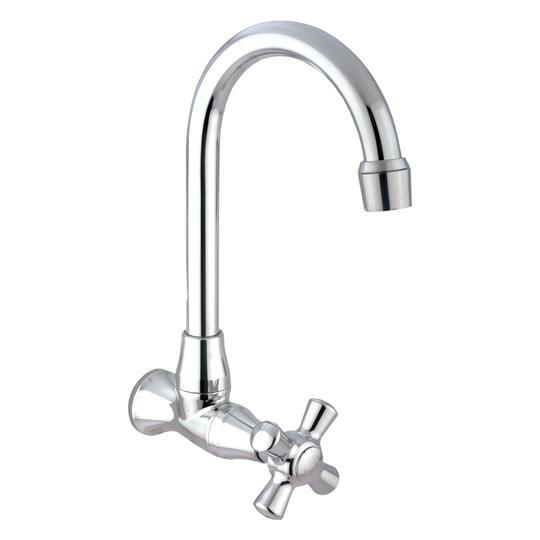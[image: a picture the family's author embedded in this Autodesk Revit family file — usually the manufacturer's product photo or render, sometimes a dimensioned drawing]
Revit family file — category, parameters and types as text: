
# Revit family: 01-0944-11 LLAVE MOVIL PARED HELVETIA
name_source: partatom
category: Plumbing Fixtures
revit_build: Autodesk Revit 2018 (Build: 20170223_1515(x64)
units: mm (PartAtom-declared; Revit-internal decimal feet)

## family parameters
Cut with Voids When Loaded = No
Host = Face
OmniClass Number = 23.31.11.00
Part Type = Normal
Room Calculation Point = No
Round Connector Dimension = Use Diameter
Shared = No

## types (1)
- 01-0944-11
    Alto Aireador = 152 mm  [stored 0.498688 ft]
    Alto cuerpo-llave = 124 mm  [stored 0.406824 ft]
    Ancho  manija = 70 mm  [stored 0.229659 ft]
    CW Connection = Yes
    Default Elevation = 0 mm  [stored 0 ft]
    Description = Monomando
    Eje - Aireador = 126 mm  [stored 0.413386 ft]
    HW Connection = Yes
    Link Ficha Tecnica = http://infotecnica.gricol.com
    Manufacturer = Gricol
    Model = 01-0944-11
    Plástico - ABS Cromado = Plastico ABS Cromado
    Product Name = LLAVE MOVIL PARED HELVETIA
    Type Image = LLAVE MOVIL PARED HELVETIA.jpg
    URL = https://www.gricol.com
    Vent Connection = No
    Waste Connection = No

note: [stored X ft] marks values corroborated as IEEE doubles in the binary element streams (Revit-internal decimal feet)

## geometry (parser evidence)
native form markers: Blend x2, Sweep x3
no freeform markers — native parametric forms only
